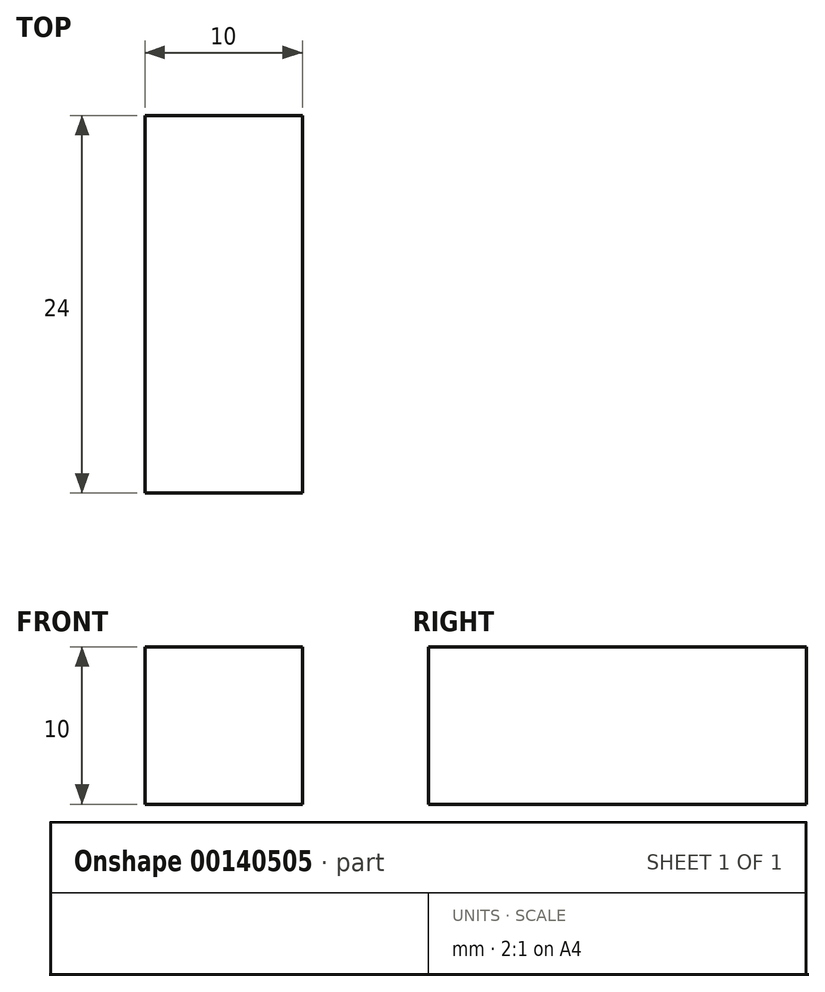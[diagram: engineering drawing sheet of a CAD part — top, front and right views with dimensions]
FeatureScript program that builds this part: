
annotation { "Feature Type Name" : "Feature", "Feature Type Description" : "" }
export const myFeature = defineFeature(function(context is Context, id is Id, definition is map)
    precondition{}
    {
        {
            var Q0;
            Q0=qCreatedBy(makeId("Front.planeOp"),FACE);
            var sketch = newSketch(context, id + "F0", { "sketchPlane" : qUnion([Q0])});
            skLineSegment(sketch, "E0.bottom", {"start": v(5, -5) * mm, "end": v(-5, -5) * mm});
            skLineSegment(sketch, "E0.top", {"start": v(5, 5) * mm, "end": v(-5, 5) * mm});
            skLineSegment(sketch, "E0.left", {"start": v(5, -5) * mm, "end": v(5, 5) * mm});
            skLineSegment(sketch, "E0.right", {"start": v(-5, -5) * mm, "end": v(-5, 5) * mm});
            skPoint(sketch, "E0.middle", {"position": v(0, 0) * mm});
            skSolve(sketch);
        }
        {
            var Q0;
            Q0=makeQuery(id+"F0.imprint","IMPRINT",FACE,{"disambiguationData":[TD([[makeQuery(id+"F0.imprint","IMPRINT",EDGE,{"derivedFrom":sQuery(id+"F0.wireOp",EDGE,"E0.bottom")}),-1.0]])]});
            extrude(context, id + "F1", {"entities" : qUnion([Q0]), "depth" : 24 * mm});
        }
    });
